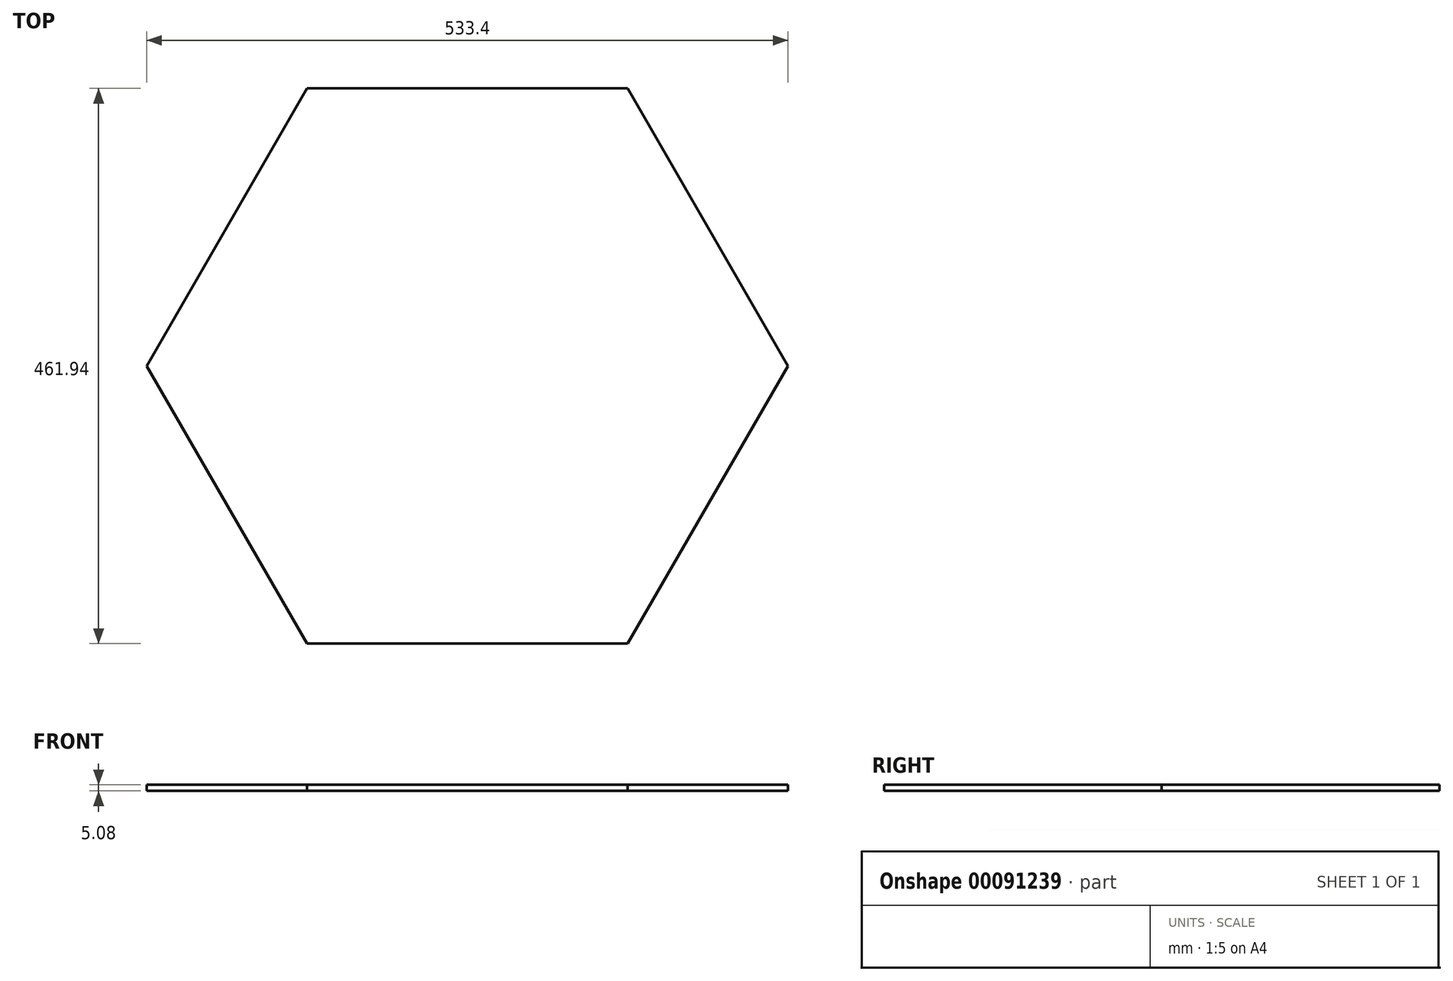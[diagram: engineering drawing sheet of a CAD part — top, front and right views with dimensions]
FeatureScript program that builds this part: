
annotation { "Feature Type Name" : "Feature", "Feature Type Description" : "" }
export const myFeature = defineFeature(function(context is Context, id is Id, definition is map)
    precondition{}
    {
        {
            var Q0;
            Q0=qCreatedBy(makeId("Top.planeOp"),FACE);
            var sketch = newSketch(context, id + "F0", { "sketchPlane" : qUnion([Q0])});
            skCircle(sketch, "E0.cCircle", {"center": v(0, 0) * mm, "radius": 230.97 * mm, "construction": true});
            skLineSegment(sketch, "E0.0", {"start": v(133.35, 230.97) * mm, "end": v(266.7, 0) * mm});
            skLineSegment(sketch, "E0.1", {"start": v(266.7, 0) * mm, "end": v(133.35, -230.97) * mm});
            skLineSegment(sketch, "E0.2", {"start": v(133.35, -230.97) * mm, "end": v(-133.35, -230.97) * mm});
            skLineSegment(sketch, "E0.3", {"start": v(-133.35, -230.97) * mm, "end": v(-266.7, 0) * mm});
            skLineSegment(sketch, "E0.4", {"start": v(-266.7, 0) * mm, "end": v(-133.35, 230.97) * mm});
            skLineSegment(sketch, "E0.5", {"start": v(-133.35, 230.97) * mm, "end": v(133.35, 230.97) * mm});
            skPoint(sketch, "E0.0.midPoint", {"position": v(200.03, 115.48) * mm});
            skLineSegment(sketch, "E1", {"start": v(-266.7, 0) * mm, "end": v(266.7, 0) * mm, "construction": true});
            skLineSegment(sketch, "E2", {"start": v(-133.35, 230.97) * mm, "end": v(133.35, -230.97) * mm, "construction": true});
            skLineSegment(sketch, "E3", {"start": v(0, -230.97) * mm, "end": v(0, 230.97) * mm, "construction": true});
            skSolve(sketch);
        }
        {
            var Q0;
            Q0=sQuery(id+"F0.wireOp",EDGE,"E0.4");
            var Q1;
            Q1=sQuery(id+"F0.wireOp",EDGE,"E0.3");
            var Q2;
            Q2=sQuery(id+"F0.wireOp",EDGE,"E0.2");
            var Q3;
            Q3=sQuery(id+"F0.wireOp",EDGE,"E0.1");
            var Q4;
            Q4=sQuery(id+"F0.wireOp",EDGE,"E0.0");
            var Q5;
            Q5=sQuery(id+"F0.wireOp",EDGE,"E0.5");
            extrude(context, id + "F1", {"bodyType" : ToolBodyType.SURFACE, "surfaceEntities" : qUnion([Q0, Q1, Q2, Q3, Q4, Q5]), "depth" : 609.6 * mm});
        }
        {
            var Q0;
            Q0 = qSketchRegion(id + "F0", true);
            extrude(context, id + "F2", {"entities" : qUnion([Q0]), "depth" : 5.08 * mm});
        }
    });
